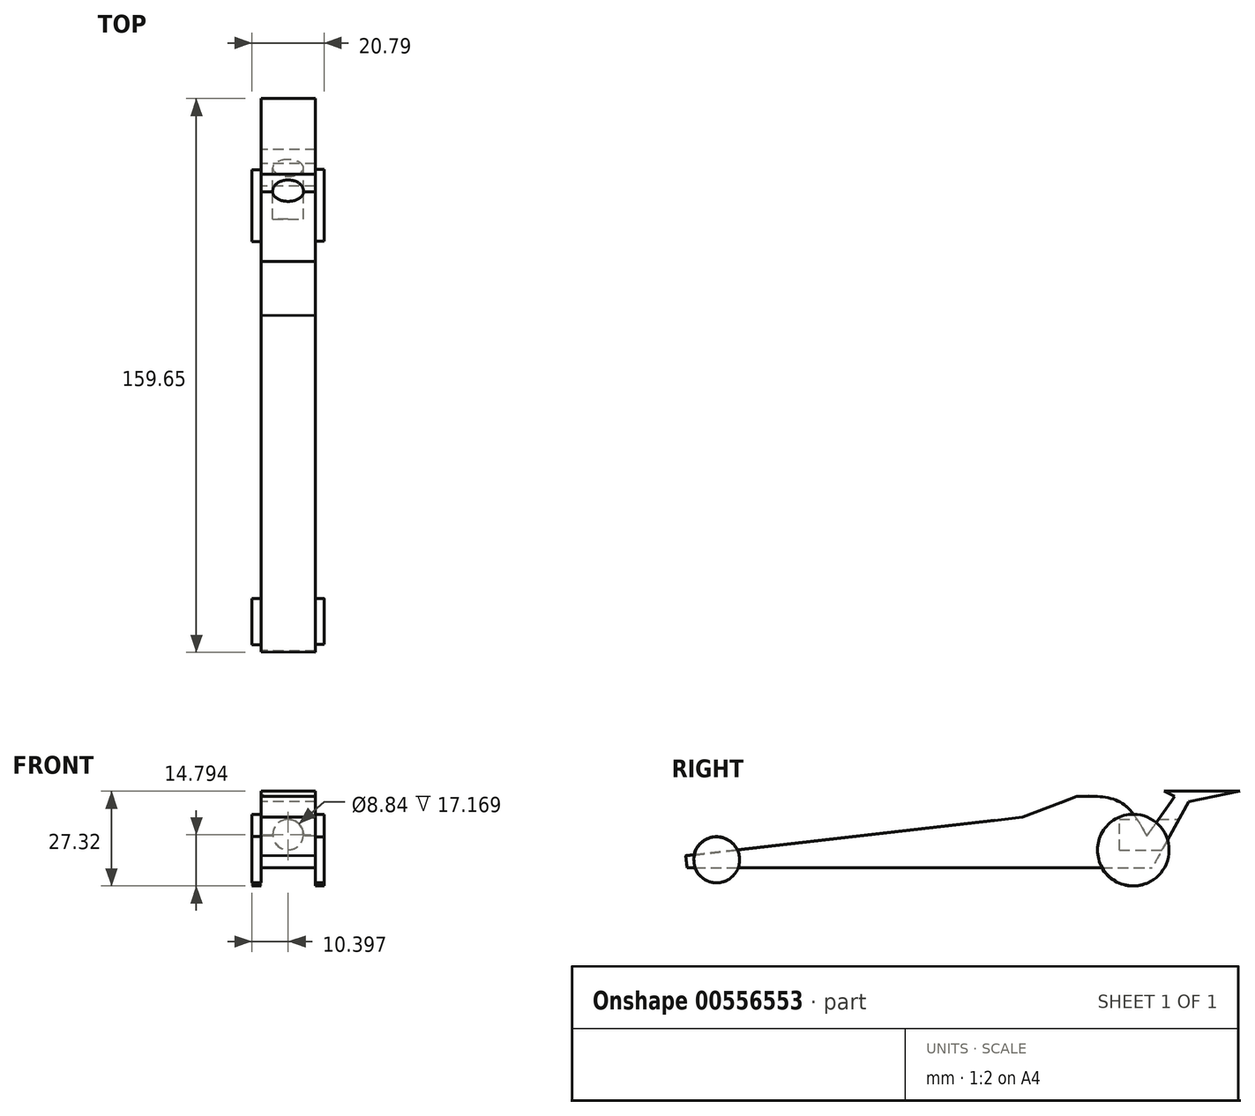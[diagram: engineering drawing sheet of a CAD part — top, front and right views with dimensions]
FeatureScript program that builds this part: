
annotation { "Feature Type Name" : "Feature", "Feature Type Description" : "" }
export const myFeature = defineFeature(function(context is Context, id is Id, definition is map)
    precondition{}
    {
        {
            var Q0;
            Q0=qCreatedBy(makeId("Right.planeOp"),FACE);
            cPlane(context, id + "F0", {"entities" : qUnion([Q0]), "cplaneType" : CPlaneType.OFFSET, "offset" : 12.5 * mm, "width" : 150 * mm, "height" : 150 * mm});
        }
        {
            var Q0;
            Q0=qCreatedBy(id+"F0.planeOp",FACE);
            var sketch = newSketch(context, id + "F1", { "sketchPlane" : qUnion([Q0])});
            skLineSegment(sketch, "E0", {"start": v(-75.2, 3.36) * mm, "end": v(21.83, 14.56) * mm});
            skLineSegment(sketch, "E1", {"start": v(-75.2, 3.36) * mm, "end": v(-74.82, 0) * mm});
            skLineSegment(sketch, "E2", {"start": v(-74.82, 0) * mm, "end": v(59.16, 0) * mm});
            skLineSegment(sketch, "E3", {"start": v(59.16, 0) * mm, "end": v(69.7, 19.03) * mm});
            skLineSegment(sketch, "E4", {"start": v(69.7, 19.03) * mm, "end": v(84.43, 22.02) * mm});
            skLineSegment(sketch, "E5", {"start": v(84.43, 22.02) * mm, "end": v(62.6, 22.02) * mm});
            skLineSegment(sketch, "E6", {"start": v(62.6, 22.02) * mm, "end": v(65.64, 20.53) * mm});
            skPoint(sketch, "E6.endSnap0", {"position": v(77.06, 20.53) * mm});
            skLineSegment(sketch, "E7", {"start": v(65.64, 20.53) * mm, "end": v(57.61, 9.14) * mm});
            skLineSegment(sketch, "E8", {"start": v(21.83, 14.56) * mm, "end": v(37.46, 20.53) * mm});
            skFitSpline(sketch, "E9", {"points": [v(37.46, 20.53) * mm, v(49.96, 18.85) * mm, v(57.61, 9.14) * mm], "startDerivative": vector(27.26, 0.72) * mm, "endDerivative": vector(13.02, -23.53) * mm});
            skSolve(sketch);
        }
        {
            var Q0;
            Q0=qCreatedBy(makeId("Right.planeOp"),FACE);
            cPlane(context, id + "F2", {"entities" : qUnion([Q0]), "cplaneType" : CPlaneType.OFFSET, "offset" : 3.2 * mm, "oppositeDirection" : true, "width" : 150 * mm, "height" : 150 * mm});
        }
        {
            var Q0;
            Q0=qCreatedBy(id+"F2.planeOp",FACE);
            var sketch = newSketch(context, id + "F3", { "sketchPlane" : qUnion([Q0])});
            skLineSegment(sketch, "E10", {"start": v(-75.07, 3.55) * mm, "end": v(21.97, 14.56) * mm});
            skLineSegment(sketch, "E11", {"start": v(-75.07, 3.55) * mm, "end": v(-74.67, 0) * mm});
            skLineSegment(sketch, "E12", {"start": v(-74.67, 0) * mm, "end": v(59.14, 0) * mm});
            skLineSegment(sketch, "E13", {"start": v(21.97, 14.56) * mm, "end": v(37.45, 20.55) * mm});
            skLineSegment(sketch, "E14", {"start": v(59.14, 0) * mm, "end": v(69.72, 19.05) * mm});
            skLineSegment(sketch, "E15", {"start": v(69.72, 19.05) * mm, "end": v(77.07, 20.54) * mm});
            skLineSegment(sketch, "E16", {"start": v(77.07, 20.54) * mm, "end": v(84.45, 22.03) * mm});
            skLineSegment(sketch, "E17", {"start": v(84.45, 22.03) * mm, "end": v(62.6, 22.03) * mm});
            skLineSegment(sketch, "E18", {"start": v(62.6, 22.03) * mm, "end": v(65.65, 20.54) * mm});
            skLineSegment(sketch, "E19", {"start": v(65.65, 20.54) * mm, "end": v(57.58, 9.13) * mm});
            skFitSpline(sketch, "E20", {"points": [v(37.45, 20.55) * mm, v(49.98, 18.86) * mm, v(57.58, 9.13) * mm], "startDerivative": vector(27.33, 0.73) * mm, "endDerivative": vector(12.92, -23.6) * mm});
            skSolve(sketch);
        }
        {
            var Q0;
            Q0=makeQuery(id+"F1.imprint","IMPRINT",FACE,{"disambiguationData":[TD([[makeQuery(id+"F1.imprint","IMPRINT",EDGE,{"derivedFrom":sQuery(id+"F1.wireOp",EDGE,"E0")}),-1.0]])]});
            var Q1;
            Q1=makeQuery(id+"F3.imprint","IMPRINT",FACE,{"disambiguationData":[TD([[makeQuery(id+"F3.imprint","IMPRINT",EDGE,{"derivedFrom":sQuery(id+"F3.wireOp",EDGE,"E10")}),-1.0]])]});
            loft(context, id + "F4", {"sheetProfilesArray" : [{ "sheetProfileEntities" : qUnion([Q0]) }, { "sheetProfileEntities" : qUnion([Q1]) }]});
        }
        {
            var Q0;
            Q0=qCreatedBy(makeId("Front.planeOp"),FACE);
            cPlane(context, id + "F5", {"entities" : qUnion([Q0]), "cplaneType" : CPlaneType.OFFSET, "offset" : 69.4 * mm, "oppositeDirection" : true, "width" : 150 * mm, "height" : 150 * mm});
        }
        {
            var Q0;
            Q0=qCreatedBy(id+"F5.planeOp",FACE);
            var sketch = newSketch(context, id + "F6", { "sketchPlane" : qUnion([Q0])});
            skCircle(sketch, "E21", {"center": v(4.6, 9.5) * mm, "radius": 4.42 * mm});
            skSolve(sketch);
        }
        {
            var Q0;
            Q0 = qSketchRegion(id + "F6", true);
            extrude(context, id + "F7", {"entities" : qUnion([Q0]), "operationType" : NewBodyOperationType.REMOVE, "depth" : 19.7 * mm, "offsetDistance" : 25 * mm});
        }
        {
            var Q0;
            Q0=qCreatedBy(makeId("Right.planeOp"),FACE);
            cPlane(context, id + "F8", {"entities" : qUnion([Q0]), "cplaneType" : CPlaneType.OFFSET, "offset" : 12.4 * mm, "width" : 150 * mm, "height" : 150 * mm});
        }
        {
            var Q0;
            Q0=qCreatedBy(id+"F8.planeOp",FACE);
            var sketch = newSketch(context, id + "F9", { "sketchPlane" : qUnion([Q0])});
            skCircle(sketch, "E22", {"center": v(-66.3, 2.24) * mm, "radius": 6.6 * mm});
            skSolve(sketch);
        }
        {
            var Q0;
            Q0=qCreatedBy(id+"F8.planeOp",FACE);
            var sketch = newSketch(context, id + "F10", { "sketchPlane" : qUnion([Q0])});
            skCircle(sketch, "E23", {"center": v(53.7, 5.07) * mm, "radius": 10.3 * mm});
            skSolve(sketch);
        }
        {
            var Q0;
            Q0=makeQuery(id+"F9.imprint","IMPRINT",FACE,{"disambiguationData":[TD([[makeQuery(id+"F9.imprint","IMPRINT",EDGE,{"derivedFrom":sQuery(id+"F9.wireOp",EDGE,"E22")}),1.0]])]});
            extrude(context, id + "F11", {"entities" : qUnion([Q0]), "operationType" : NewBodyOperationType.ADD, "depth" : 1.4 * mm, "offsetDistance" : 25 * mm});
        }
        {
            var Q0;
            Q0 = qSketchRegion(id + "F9", true);
            var Q1;
            Q1=makeQuery(id+"F10.imprint","IMPRINT",FACE,{"disambiguationData":[TD([[makeQuery(id+"F10.imprint","IMPRINT",EDGE,{"derivedFrom":sQuery(id+"F10.wireOp",EDGE,"E23")}),1.0]])]});
            extrude(context, id + "F12", {"entities" : qUnion([Q0, Q1]), "operationType" : NewBodyOperationType.ADD, "depth" : 2.6 * mm, "offsetDistance" : 25 * mm});
        }
        {
            var Q0;
            Q0=qCreatedBy(makeId("Right.planeOp"),FACE);
            cPlane(context, id + "F13", {"entities" : qUnion([Q0]), "cplaneType" : CPlaneType.OFFSET, "offset" : 3.19 * mm, "oppositeDirection" : true, "width" : 150 * mm, "height" : 150 * mm});
        }
        {
            var Q0;
            Q0=qCreatedBy(id+"F13.planeOp",FACE);
            var sketch = newSketch(context, id + "F14", { "sketchPlane" : qUnion([Q0])});
            skCircle(sketch, "E24", {"center": v(-66.35, 2.26) * mm, "radius": 6.66 * mm});
            skCircle(sketch, "E25", {"center": v(53.6, 5.05) * mm, "radius": 10.34 * mm});
            skSolve(sketch);
        }
        {
            var Q0;
            Q0 = qSketchRegion(id + "F14", true);
            extrude(context, id + "F15", {"entities" : qUnion([Q0]), "operationType" : NewBodyOperationType.ADD, "oppositeDirection" : true, "depth" : 2.6 * mm, "offsetDistance" : 25 * mm});
        }
    });
